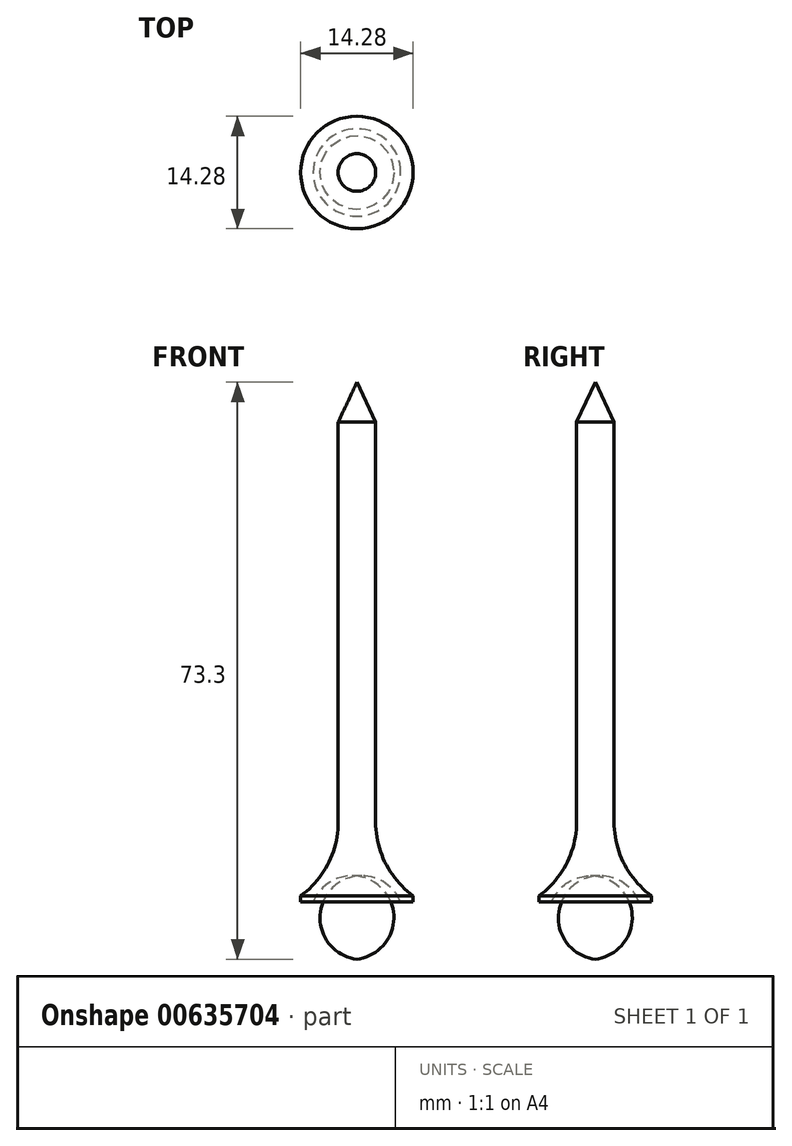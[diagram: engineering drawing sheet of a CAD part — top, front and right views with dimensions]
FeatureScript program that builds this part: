
annotation { "Feature Type Name" : "Feature", "Feature Type Description" : "" }
export const myFeature = defineFeature(function(context is Context, id is Id, definition is map)
    precondition{}
    {
        {
            var Q0;
            Q0=qCreatedBy(makeId("Front.planeOp"),FACE);
            var sketch = newSketch(context, id + "F0", { "sketchPlane" : qUnion([Q0])});
            skLineSegment(sketch, "E0", {"start": v(0, 0) * mm, "end": v(5.56, 0) * mm, "construction": true});
            skLineSegment(sketch, "E1", {"start": v(5.56, 0) * mm, "end": v(7.14, 0) * mm});
            skLineSegment(sketch, "E2", {"start": v(0, 0) * mm, "end": v(0, 3.3) * mm, "construction": true});
            skArc(sketch, "E3", {"start": v(5.56, 0) * mm, "mid": v(3.34, 2.6) * mm, "end": v(0, 3.3) * mm});
            skLineSegment(sketch, "E4.bottom", {"start": v(0, 0) * mm, "end": v(4.76, 0) * mm, "construction": true});
            skLineSegment(sketch, "E5.bottom", {"start": v(0, 0) * mm, "end": v(2.38, 0) * mm, "construction": true});
            skLineSegment(sketch, "E5.top", {"start": v(0, 10.16) * mm, "end": v(2.38, 10.16) * mm, "construction": true});
            skLineSegment(sketch, "E5.left", {"start": v(0, 0) * mm, "end": v(0, 10.16) * mm, "construction": true});
            skLineSegment(sketch, "E5.right", {"start": v(2.38, 0) * mm, "end": v(2.38, 10.16) * mm, "construction": true});
            skLineSegment(sketch, "E6", {"start": v(2.38, 10.16) * mm, "end": v(2.38, 60.96) * mm});
            skLineSegment(sketch, "E7", {"start": v(0, 0) * mm, "end": v(0, 66.04) * mm});
            skPoint(sketch, "E7.endSnap0", {"position": v(0, 5.08) * mm});
            skLineSegment(sketch, "E8", {"start": v(2.38, 60.96) * mm, "end": v(0, 66.04) * mm});
            skLineSegment(sketch, "E9", {"start": v(0, 0) * mm, "end": v(0, 100.57) * mm, "construction": true});
            skPoint(sketch, "E9.endSnap0", {"position": v(0, 33.02) * mm});
            skLineSegment(sketch, "E10", {"start": v(7.14, 0) * mm, "end": v(7.14, 0.8) * mm});
            skArc(sketch, "E11", {"start": v(2.38, 10.16) * mm, "mid": v(3.64, 4.9) * mm, "end": v(7.14, 0.8) * mm});
            skSolve(sketch);
        }
        {
            var Q0;
            Q0 = qSketchRegion(id + "F0", true);
            var Q1;
            Q1=sQuery(id+"F0.wireOp",EDGE,"E9");
            revolve(context, id + "F1", {"entities" : qUnion([Q0]), "axis" : qUnion([Q1]), "revolveType" : RevolveType.FULL});
        }
    });
